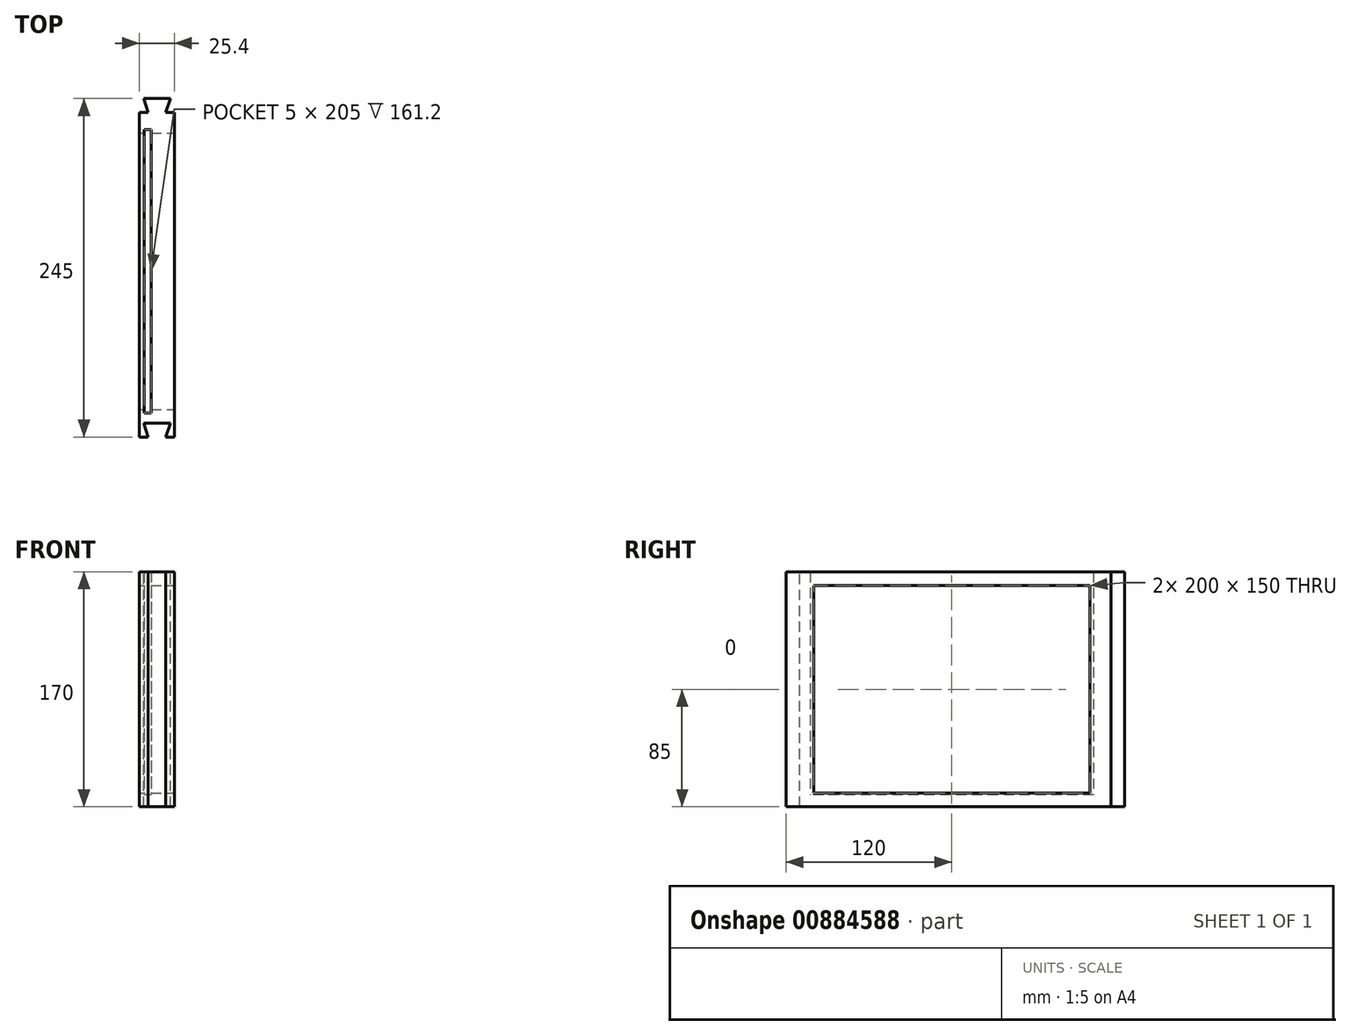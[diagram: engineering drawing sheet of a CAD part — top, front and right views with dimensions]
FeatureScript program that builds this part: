
annotation { "Feature Type Name" : "Feature", "Feature Type Description" : "" }
export const myFeature = defineFeature(function(context is Context, id is Id, definition is map)
    precondition{}
    {
        {
            var Q0;
            Q0=qCreatedBy(makeId("Right.planeOp"),FACE);
            var sketch = newSketch(context, id + "F0", { "sketchPlane" : qUnion([Q0])});
            skLineSegment(sketch, "E0.bottom", {"start": v(125, 85) * mm, "end": v(-125, 85) * mm});
            skLineSegment(sketch, "E0.top", {"start": v(125, -85) * mm, "end": v(-125, -85) * mm});
            skLineSegment(sketch, "E0.left", {"start": v(125, 85) * mm, "end": v(125, -85) * mm});
            skLineSegment(sketch, "E0.right", {"start": v(-125, 85) * mm, "end": v(-125, -85) * mm});
            skPoint(sketch, "E0.middle", {"position": v(0, 0) * mm});
            skSolve(sketch);
        }
        {
            var Q0;
            Q0 = qSketchRegion(id + "F0", true);
            extrude(context, id + "F1", {"entities" : qUnion([Q0]), "depth" : 12.7 * mm, "offsetDistance" : 25.4 * mm, "hasSecondDirection" : true, "secondDirectionOppositeDirection" : true, "secondDirectionDepth" : 12.7 * mm});
        }
        {
            var Q0;
            Q0=qCreatedBy(makeId("Top.planeOp"),FACE);
            var sketch = newSketch(context, id + "F2", { "sketchPlane" : qUnion([Q0])});
            skLineSegment(sketch, "E1.bottom", {"start": v(-4.2, 102.5) * mm, "end": v(-9.2, 102.5) * mm});
            skLineSegment(sketch, "E1.top", {"start": v(-4.2, -102.5) * mm, "end": v(-9.2, -102.5) * mm});
            skLineSegment(sketch, "E1.left", {"start": v(-4.2, 102.5) * mm, "end": v(-4.2, -102.5) * mm});
            skLineSegment(sketch, "E1.right", {"start": v(-9.2, 102.5) * mm, "end": v(-9.2, -102.5) * mm});
            skPoint(sketch, "E1.middle", {"position": v(-6.7, 0) * mm});
            skSolve(sketch);
        }
        {
            var Q0;
            Q0 = qSketchRegion(id + "F2", true);
            extrude(context, id + "F3", {"entities" : qUnion([Q0]), "operationType" : NewBodyOperationType.REMOVE, "endBound" : BoundingType.THROUGH_ALL, "depth" : 50.8 * mm, "offsetDistance" : 25.4 * mm, "hasSecondDirection" : true, "secondDirectionOppositeDirection" : true, "secondDirectionDepth" : 76.2 * mm});
        }
        {
            var Q0;
            Q0=makeQuery(id+"F1.opExtrude","CAP_FACE",FACE,{"disambiguationData":[OSD([sQuery(id+"F0.wireOp",EDGE,"E0.bottom"),sQuery(id+"F0.wireOp",EDGE,"E0.top"),sQuery(id+"F0.wireOp",EDGE,"E0.left"),sQuery(id+"F0.wireOp",EDGE,"E0.right")])],"isStart":false});
            var sketch = newSketch(context, id + "F4", { "sketchPlane" : qUnion([Q0])});
            skLineSegment(sketch, "E2.bottom", {"start": v(100, 75) * mm, "end": v(-100, 75) * mm});
            skLineSegment(sketch, "E2.top", {"start": v(100, -75) * mm, "end": v(-100, -75) * mm});
            skLineSegment(sketch, "E2.left", {"start": v(100, 75) * mm, "end": v(100, -75) * mm});
            skLineSegment(sketch, "E2.right", {"start": v(-100, 75) * mm, "end": v(-100, -75) * mm});
            skPoint(sketch, "E2.middle", {"position": v(0, 0) * mm});
            skSolve(sketch);
        }
        {
            var Q0;
            Q0 = qSketchRegion(id + "F4", true);
            extrude(context, id + "F5", {"entities" : qUnion([Q0]), "operationType" : NewBodyOperationType.REMOVE, "endBound" : BoundingType.THROUGH_ALL, "oppositeDirection" : true, "depth" : 25.4 * mm, "offsetDistance" : 25.4 * mm, "hasSecondDirection" : true, "secondDirectionBound" : SecondDirectionBoundingType.THROUGH_ALL, "secondDirectionOppositeDirection" : false, "secondDirectionDepth" : 25.4 * mm});
        }
        {
            var Q0;
            Q0=qCreatedBy(makeId("Top.planeOp"),FACE);
            var Q1;
            Q1=qCreatedBy(makeId("Top.planeOp"),FACE);
            var Q2;
            Q2=makeQuery(id+"F1.opExtrude","SWEPT_FACE",FACE,{"disambiguationData":[OSD([sQuery(id+"F0.wireOp",EDGE,"E0.left")])]});
            var Q3;
            Q3=makeQuery(id+"F1.opExtrude","SWEPT_FACE",FACE,{"disambiguationData":[OSD([sQuery(id+"F0.wireOp",EDGE,"E0.bottom")])]});
            var Q4;
            Q4=makeQuery(id+"F1.opExtrude","SWEPT_FACE",FACE,{"disambiguationData":[OSD([sQuery(id+"F0.wireOp",EDGE,"E0.bottom")])]});
            var Q5;
            Q5=qCreatedBy(makeId("Top.planeOp"),FACE);
            var Q6;
            Q6=qCreatedBy(makeId("Top.planeOp"),FACE);
            var Q7;
            Q7=qCreatedBy(makeId("Top.planeOp"),FACE);
            var sketch = newSketch(context, id + "F6", { "sketchPlane" : qUnion([Q0, Q1, Q2, Q3, Q4, Q5, Q6, Q7])});
            skLineSegment(sketch, "E3.bottom", {"start": v(12.7, -125) * mm, "end": v(-12.7, -125) * mm});
            skLineSegment(sketch, "E3.left", {"start": v(12.7, -125) * mm, "end": v(12.7, -120) * mm});
            skLineSegment(sketch, "E3.right", {"start": v(-12.7, -125) * mm, "end": v(-12.7, -120) * mm});
            skPoint(sketch, "E3.middle", {"position": v(0, -122.5) * mm});
            skLineSegment(sketch, "E4", {"start": v(-6.35, -120) * mm, "end": v(-9.7, -110) * mm});
            skLineSegment(sketch, "E5", {"start": v(-9.7, -110) * mm, "end": v(0, -110) * mm});
            skLineSegment(sketch, "E6.MirrorCS", {"start": v(9.7, -110) * mm, "end": v(0, -110) * mm});
            skLineSegment(sketch, "E7.MirrorCS", {"start": v(6.35, -120) * mm, "end": v(9.7, -110) * mm});
            skLineSegment(sketch, "E8", {"start": v(-12.7, -120) * mm, "end": v(-6.35, -120) * mm});
            skLineSegment(sketch, "E9", {"start": v(6.35, -120) * mm, "end": v(12.7, -120) * mm});
            skPoint(sketch, "E10.middle", {"position": v(43.05, -83.4) * mm});
            skLineSegment(sketch, "E11", {"start": v(-6.35, 115) * mm, "end": v(-9.7, 125) * mm});
            skLineSegment(sketch, "E12", {"start": v(-9.7, 125) * mm, "end": v(-2.67, 125) * mm});
            skLineSegment(sketch, "E13.MirrorCS", {"start": v(9.7, 125) * mm, "end": v(-2.67, 125) * mm});
            skLineSegment(sketch, "E14.MirrorCS", {"start": v(6.35, 115) * mm, "end": v(9.7, 125) * mm});
            skLineSegment(sketch, "E15", {"start": v(-12.7, 115) * mm, "end": v(-6.35, 115) * mm});
            skLineSegment(sketch, "E16", {"start": v(6.35, 115) * mm, "end": v(12.7, 115) * mm});
            skLineSegment(sketch, "E17", {"start": v(-12.7, 115) * mm, "end": v(-12.7, 125) * mm});
            skLineSegment(sketch, "E18", {"start": v(-12.7, 125) * mm, "end": v(12.7, 125) * mm});
            skLineSegment(sketch, "E19", {"start": v(12.7, 125) * mm, "end": v(12.7, 115) * mm});
            skLineSegment(sketch, "E20", {"start": v(9.7, -110) * mm, "end": v(12.7, -110) * mm, "construction": true});
            skLineSegment(sketch, "E21", {"start": v(12.7, -110) * mm, "end": v(12.7, -120) * mm, "construction": true});
            skLineSegment(sketch, "E22", {"start": v(-9.7, -110) * mm, "end": v(-12.7, -110) * mm, "construction": true});
            skLineSegment(sketch, "E23", {"start": v(-12.7, -110) * mm, "end": v(-12.7, -120) * mm, "construction": true});
            skSolve(sketch);
        }
        {
            var Q0;
            Q0 = qSketchRegion(id + "F6", true);
            extrude(context, id + "F7", {"entities" : qUnion([Q0]), "operationType" : NewBodyOperationType.REMOVE, "endBound" : BoundingType.THROUGH_ALL, "oppositeDirection" : true, "depth" : 25 * mm, "offsetDistance" : 25 * mm, "hasSecondDirection" : true, "secondDirectionBound" : SecondDirectionBoundingType.THROUGH_ALL, "secondDirectionOppositeDirection" : false, "secondDirectionDepth" : 25 * mm});
        }
    });
